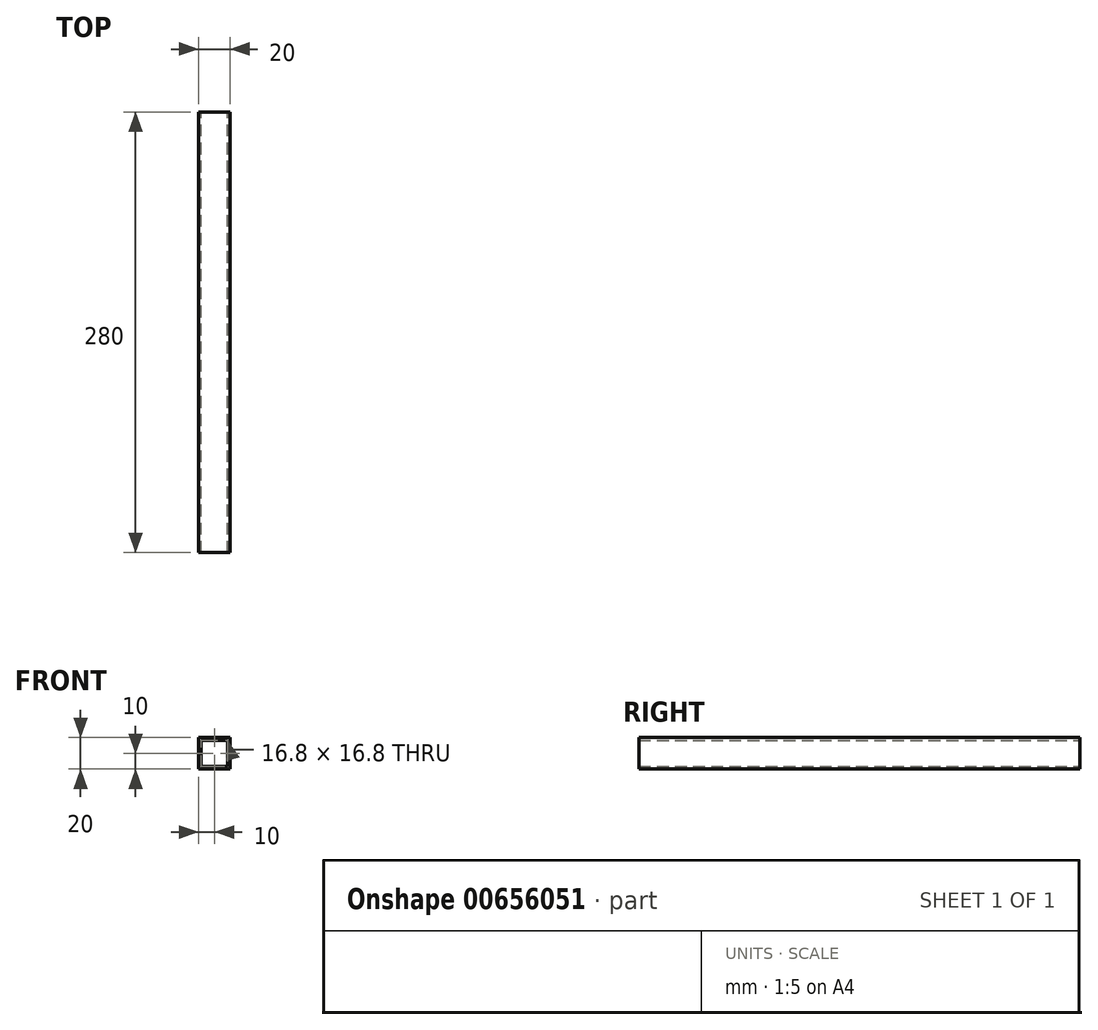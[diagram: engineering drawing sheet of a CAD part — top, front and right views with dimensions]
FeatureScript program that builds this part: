
annotation { "Feature Type Name" : "Feature", "Feature Type Description" : "" }
export const myFeature = defineFeature(function(context is Context, id is Id, definition is map)
    precondition{}
    {
        {
            var Q0;
            Q0=qCreatedBy(makeId("Front.planeOp"),FACE);
            var sketch = newSketch(context, id + "F0", { "sketchPlane" : qUnion([Q0])});
            skLineSegment(sketch, "E0.bottom", {"start": v(0, 0) * mm, "end": v(20, 0) * mm});
            skLineSegment(sketch, "E0.top", {"start": v(0, -20) * mm, "end": v(20, -20) * mm});
            skLineSegment(sketch, "E0.left", {"start": v(0, 0) * mm, "end": v(0, -20) * mm});
            skLineSegment(sketch, "E0.right", {"start": v(20, 0) * mm, "end": v(20, -20) * mm});
            skLineSegment(sketch, "E1.0", {"start": v(1.6, -1.6) * mm, "end": v(18.4, -1.6) * mm});
            skLineSegment(sketch, "E1.1", {"start": v(1.6, -1.6) * mm, "end": v(1.6, -18.4) * mm});
            skLineSegment(sketch, "E1.2", {"start": v(1.6, -18.4) * mm, "end": v(18.4, -18.4) * mm});
            skLineSegment(sketch, "E1.3", {"start": v(18.4, -1.6) * mm, "end": v(18.4, -18.4) * mm});
            skSolve(sketch);
        }
        {
            var Q0;
            Q0=makeQuery(id+"F0.imprint","IMPRINT",FACE,{"disambiguationData":[TD([[makeQuery(id+"F0.imprint","IMPRINT",EDGE,{"derivedFrom":sQuery(id+"F0.wireOp",EDGE,"E0.bottom")}),-1.0]])]});
            extrude(context, id + "F1", {"entities" : qUnion([Q0]), "depth" : 280 * mm, "offsetDistance" : 25.4 * mm});
        }
    });
